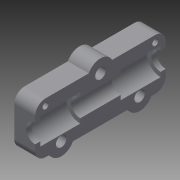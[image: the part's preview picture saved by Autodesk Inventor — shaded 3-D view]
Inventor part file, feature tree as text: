
AUTODESK INVENTOR PART (.ipt)
format: ipt  version: 2013 (Build 170138000, 138)  size: 479,232 bytes
history: native  units: mm
features: extrude x13, sketch x13, other x6, fillet x4, mirror x2, projected_geometry x2
ambient origin geometry x8: Origin, YZ Plane, XZ Plane, XY Plane, X Axis, Y Axis, Z Axis, Center Point
feature tree (40):
  other  "Těleso1"
  extrude  "Vysunutí1"  Depth=32.0mm
  extrude  "Vysunutí2"  Depth=55.0mm
  extrude  "Vysunutí3"  Depth=100.0mm TaperAngle=0.0deg
  extrude  "Vysunutí4"  Depth=30.0mm
  fillet  "Zaoblení1"  Radius=60.0mm
  extrude  "Vysunutí5"  Depth=8.1mm
  extrude  "Vysunutí6"  Depth=100.0mm TaperAngle=0.0deg
  mirror  "Zrcadlit1"
  extrude  "Vysunutí7"  Depth=21.0mm
  extrude  "Vysunutí8"  Depth=30.5mm
  fillet  "Zaoblení2"  Radius=30.5mm
  extrude  "Vysunutí9"  Depth=4.0mm
  extrude  "Vysunutí10"  Depth=100.0mm TaperAngle=0.0deg
  extrude  "Vysunutí11"  Depth=10.0mm
  fillet  "Zaoblení3"  Radius=8.0mm
  extrude  "Vysunutí12"  Depth=8.0mm
  fillet  "Zaoblení4"  Radius=8.0mm
  mirror  "Zrcadlit2"
  extrude  "Vysunutí13"  Depth=100.0mm TaperAngle=0.0deg
  sketch  "Náčrt1"
  sketch  "Náčrt2"
  sketch  "Náčrt3"
  sketch  "Náčrt4"
  sketch  "Náčrt5"
  sketch  "Náčrt6"
  sketch  "Náčrt7"
  other  "Pole Těleso1:1"
  other  "Těleso2"
  sketch  "Náčrt8"
  other  "Těleso3"
  sketch  "Náčrt9"
  projected_geometry  "Promítnutá smyčka1"
  sketch  "Náčrt10"
  sketch  "Náčrt11"
  sketch  "Náčrt12"
  projected_geometry  "Promítnutá smyčka2"
  other  "Pole Těleso3:2"
  other  "Těleso4"
  sketch  "Náčrt13"
